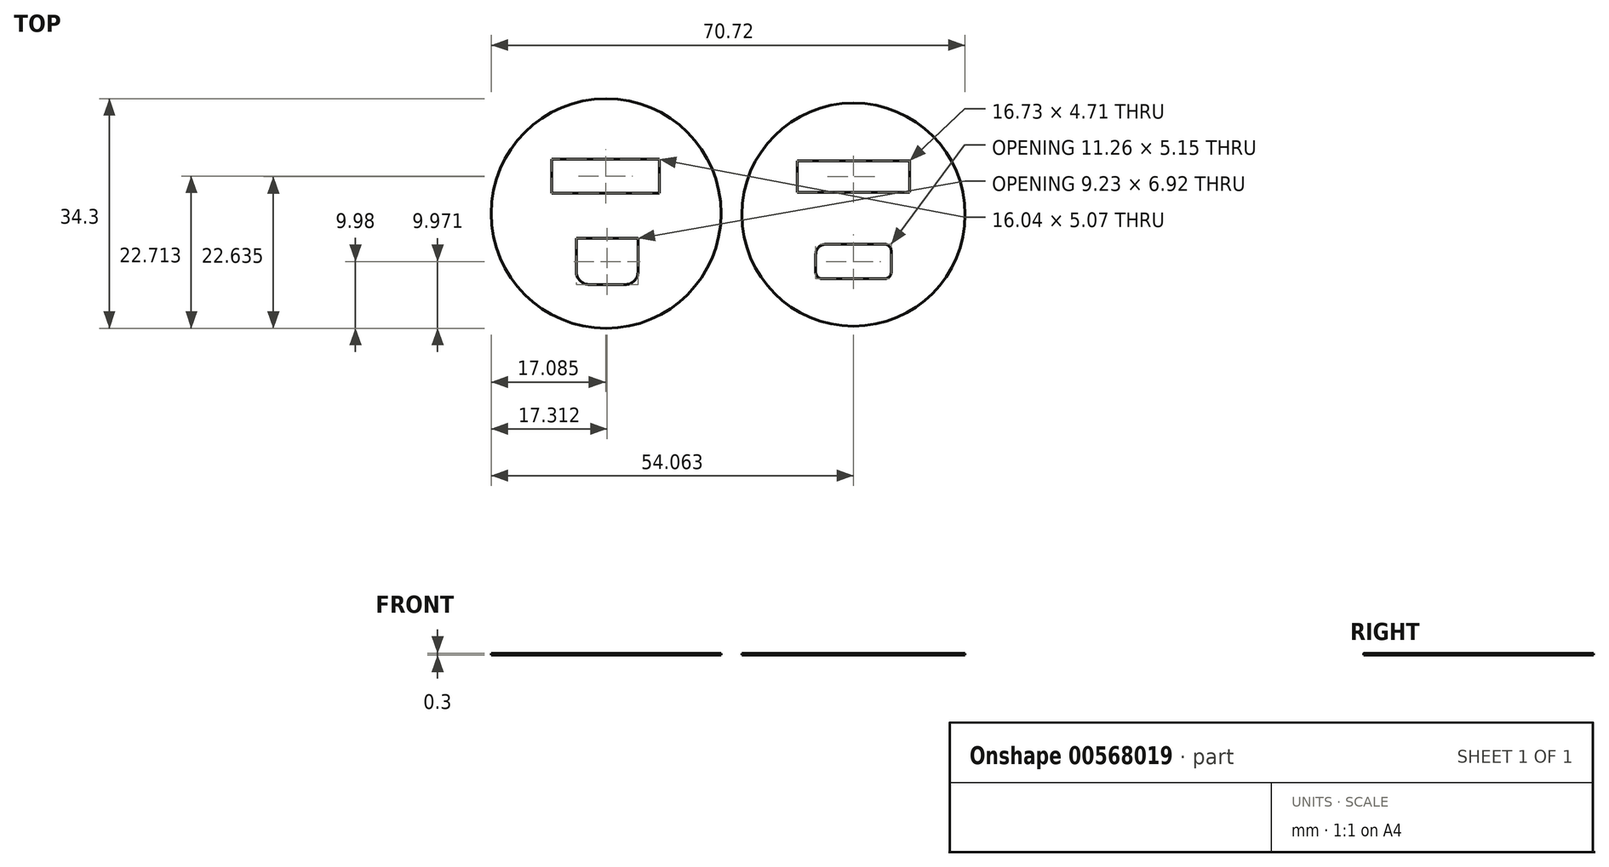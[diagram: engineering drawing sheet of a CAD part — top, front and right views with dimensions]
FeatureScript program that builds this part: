
annotation { "Feature Type Name" : "Feature", "Feature Type Description" : "" }
export const myFeature = defineFeature(function(context is Context, id is Id, definition is map)
    precondition{}
    {
        {
            var Q0;
            Q0=qCreatedBy(makeId("Top.planeOp"),FACE);
            var sketch = newSketch(context, id + "F0", { "sketchPlane" : qUnion([Q0])});
            skCircle(sketch, "E0", {"center": v(36.83, 3.33) * mm, "radius": 16.66 * mm});
            skLineSegment(sketch, "E1.bottom", {"start": v(45.2, 6.63) * mm, "end": v(28.47, 6.63) * mm});
            skLineSegment(sketch, "E1.top", {"start": v(45.2, 11.34) * mm, "end": v(28.47, 11.34) * mm});
            skLineSegment(sketch, "E1.left", {"start": v(45.2, 6.63) * mm, "end": v(45.2, 11.34) * mm});
            skLineSegment(sketch, "E1.right", {"start": v(28.47, 6.63) * mm, "end": v(28.47, 11.34) * mm});
            skPoint(sketch, "E1.middle", {"position": v(36.83, 8.99) * mm});
            skLineSegment(sketch, "E2.bottom", {"start": v(41.46, -6.26) * mm, "end": v(32.2, -6.26) * mm});
            skLineSegment(sketch, "E2.top", {"start": v(41.46, -1.1) * mm, "end": v(32.7, -1.1) * mm});
            skLineSegment(sketch, "E2.left", {"start": v(42.46, -5.26) * mm, "end": v(42.46, -2.1) * mm});
            skLineSegment(sketch, "E2.right", {"start": v(31.2, -5.26) * mm, "end": v(31.2, -2.6) * mm});
            skPoint(sketch, "E2.middle", {"position": v(36.83, -3.68) * mm});
            skPoint(sketch, "E3.visualSharp", {"position": v(31.2, -1.1) * mm});
            skArc(sketch, "E3.filletArc", {"start": v(32.7, -1.1) * mm, "mid": v(31.64, -1.54) * mm, "end": v(31.2, -2.6) * mm});
            skPoint(sketch, "E4.visualSharp", {"position": v(42.46, -1.1) * mm});
            skArc(sketch, "E4.filletArc", {"start": v(42.46, -2.1) * mm, "mid": v(42.17, -1.4) * mm, "end": v(41.46, -1.1) * mm});
            skPoint(sketch, "E5.visualSharp", {"position": v(42.46, -6.26) * mm});
            skArc(sketch, "E5.filletArc", {"start": v(41.46, -6.26) * mm, "mid": v(42.17, -5.96) * mm, "end": v(42.46, -5.26) * mm});
            skPoint(sketch, "E6.visualSharp", {"position": v(31.2, -6.26) * mm});
            skArc(sketch, "E6.filletArc", {"start": v(31.2, -5.26) * mm, "mid": v(31.5, -5.96) * mm, "end": v(32.2, -6.26) * mm});
            skCircle(sketch, "E7", {"center": v(-0.08, 3.5) * mm, "radius": 17.15 * mm});
            skLineSegment(sketch, "E8.bottom", {"start": v(7.88, 11.6) * mm, "end": v(-8.17, 11.6) * mm});
            skLineSegment(sketch, "E8.top", {"start": v(7.88, 6.53) * mm, "end": v(-8.17, 6.53) * mm});
            skLineSegment(sketch, "E8.left", {"start": v(7.88, 11.6) * mm, "end": v(7.88, 6.53) * mm});
            skLineSegment(sketch, "E8.right", {"start": v(-8.17, 11.6) * mm, "end": v(-8.17, 6.53) * mm});
            skLineSegment(sketch, "E9.bottom", {"start": v(-4.53, -0.2) * mm, "end": v(4.7, -0.2) * mm});
            skLineSegment(sketch, "E9.top", {"start": v(-2.53, -7.13) * mm, "end": v(2.7, -7.13) * mm});
            skLineSegment(sketch, "E9.left", {"start": v(-4.53, -0.2) * mm, "end": v(-4.53, -5.13) * mm});
            skLineSegment(sketch, "E9.right", {"start": v(4.7, -0.2) * mm, "end": v(4.7, -5.13) * mm});
            skPoint(sketch, "E10.visualSharp", {"position": v(-4.53, -7.13) * mm});
            skArc(sketch, "E10.filletArc", {"start": v(-4.53, -5.13) * mm, "mid": v(-3.95, -6.55) * mm, "end": v(-2.53, -7.13) * mm});
            skPoint(sketch, "E11.visualSharp", {"position": v(4.7, -7.13) * mm});
            skArc(sketch, "E11.filletArc", {"start": v(2.7, -7.13) * mm, "mid": v(4.11, -6.55) * mm, "end": v(4.7, -5.13) * mm});
            skSolve(sketch);
        }
        {
            var Q0;
            Q0=makeQuery(id+"F0.imprint","IMPRINT",FACE,{"disambiguationData":[TD([[makeQuery(id+"F0.imprint","IMPRINT",EDGE,{"derivedFrom":sQuery(id+"F0.wireOp",EDGE,"E7")}),1.0]])]});
            var Q1;
            Q1=makeQuery(id+"F0.imprint","IMPRINT",FACE,{"disambiguationData":[TD([[makeQuery(id+"F0.imprint","IMPRINT",EDGE,{"derivedFrom":sQuery(id+"F0.wireOp",EDGE,"E0")}),1.0]])]});
            extrude(context, id + "F1", {"entities" : qUnion([Q0, Q1]), "depth" : 0.3 * mm, "offsetDistance" : 25 * mm});
        }
    });
